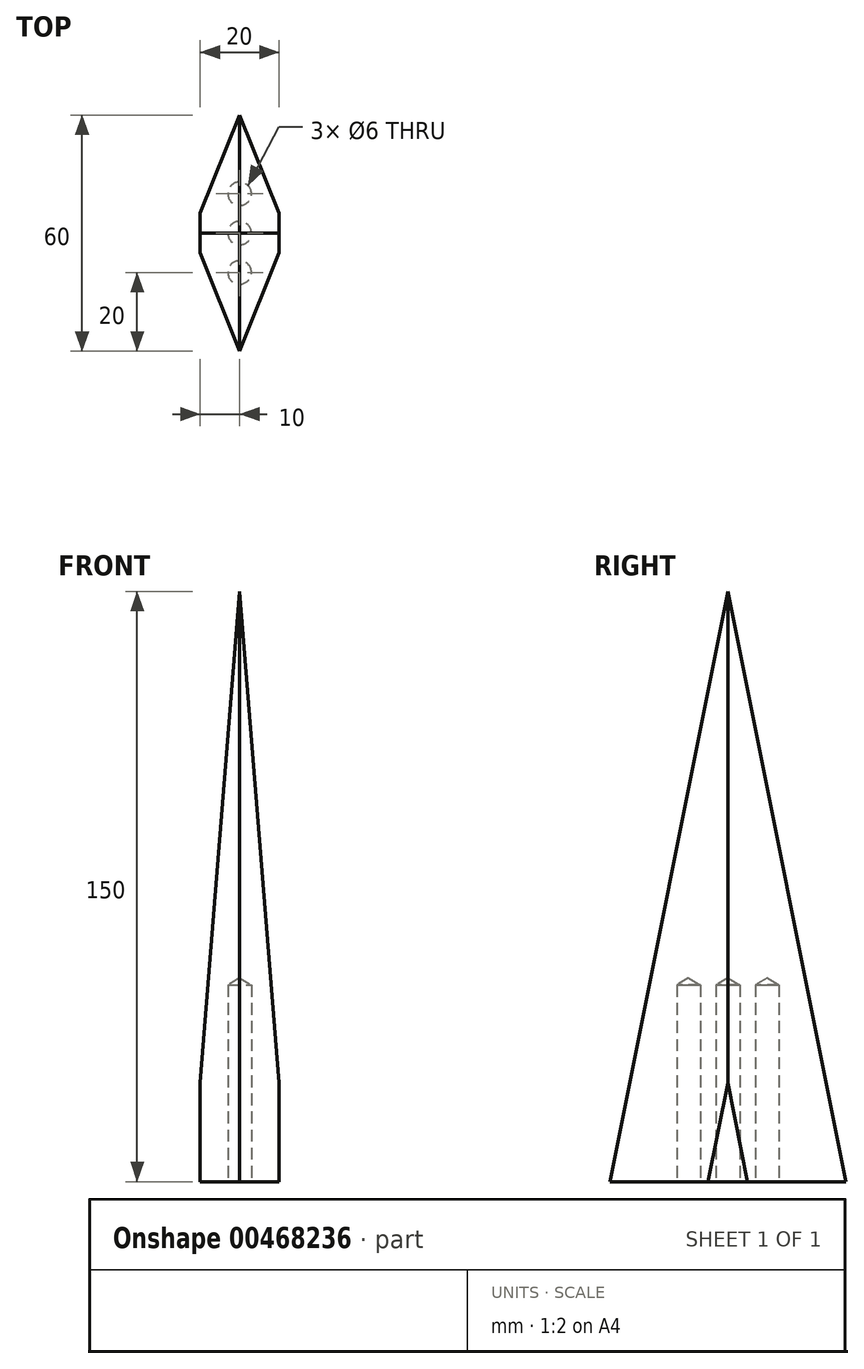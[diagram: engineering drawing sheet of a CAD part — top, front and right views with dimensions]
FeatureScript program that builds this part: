
annotation { "Feature Type Name" : "Feature", "Feature Type Description" : "" }
export const myFeature = defineFeature(function(context is Context, id is Id, definition is map)
    precondition{}
    {
        {
            var Q0;
            Q0=qCreatedBy(makeId("Top.planeOp"),FACE);
            var sketch = newSketch(context, id + "F0", { "sketchPlane" : qUnion([Q0])});
            skLineSegment(sketch, "E0.bottom", {"start": v(10, -30) * mm, "end": v(-10, -30) * mm});
            skLineSegment(sketch, "E0.top", {"start": v(10, 30) * mm, "end": v(-10, 30) * mm});
            skLineSegment(sketch, "E0.left", {"start": v(10, -30) * mm, "end": v(10, 30) * mm});
            skLineSegment(sketch, "E0.right", {"start": v(-10, -30) * mm, "end": v(-10, 30) * mm});
            skPoint(sketch, "E0.middle", {"position": v(0, 0) * mm});
            skLineSegment(sketch, "E1", {"start": v(0, 0) * mm, "end": v(0, 10) * mm});
            skLineSegment(sketch, "E2", {"start": v(0, 0) * mm, "end": v(0, -10) * mm});
            skSolve(sketch);
        }
        {
            var Q0;
            Q0=makeQuery(id+"F0.imprint","IMPRINT",FACE,{"disambiguationData":[TD([[makeQuery(id+"F0.imprint","IMPRINT",EDGE,{"derivedFrom":sQuery(id+"F0.wireOp",EDGE,"E0.bottom")}),-1.0]])]});
            extrude(context, id + "F1", {"entities" : qUnion([Q0]), "depth" : 150 * mm});
        }
        {
            var Q0;
            Q0=sQuery(id+"F0.wireOp",VERTEX,"E1.end");
            var Q1;
            Q1=sQuery(id+"F0.wireOp",VERTEX,"E0.middle");
            var Q2;
            Q2=sQuery(id+"F0.wireOp",VERTEX,"E2.end");
            var Q3;
            Q3=makeQuery(id+"F1.opExtrude","SWEPT_BODY",BODY,{"disambiguationData":[OSD([sQuery(id+"F0.wireOp",EDGE,"E0.bottom"),sQuery(id+"F0.wireOp",EDGE,"E0.top"),sQuery(id+"F0.wireOp",EDGE,"E0.left"),sQuery(id+"F0.wireOp",EDGE,"E0.right")])]});
            hole(context, id + "F2", {"style" : HoleStyle.SIMPLE, "endStyle" : HoleEndStyle.BLIND, "oppositeDirection" : true, "holeDiameter" : 6 * mm, "holeDepth" : 50 * mm, "isTappedThrough" : true, "tappedDepth" : 12 * mm, "tapClearance" : 3, "locations" : qUnion([Q0, Q1, Q2]), "scope" : qUnion([Q3])});
        }
        {
            var Q0;
            Q0=makeQuery(id+"F1.opExtrude","CAP_EDGE",EDGE,{"disambiguationData":[OSD([sQuery(id+"F0.wireOp",EDGE,"E0.bottom")])],"isStart":false});
            var Q1;
            Q1=makeQuery(id+"F1.opExtrude","CAP_EDGE",EDGE,{"disambiguationData":[OSD([sQuery(id+"F0.wireOp",EDGE,"E0.top")])],"isStart":false});
            chamfer(context, id + "F3", {"entities" : qUnion([Q0, Q1]), "chamferType" : ChamferType.TWO_OFFSETS, "width1" : 150 * mm, "oppositeDirection" : false, "width2" : 30 * mm, "tangentPropagation" : true});
        }
        {
            var Q0;
            Q0=makeQuery(id+"F3.opChamfer","BLEND_EDGE",EDGE,{"blendedFrom":[makeQuery(id+"F1.opExtrude","CAP_EDGE",EDGE,{"disambiguationData":[OSD([sQuery(id+"F0.wireOp",EDGE,"E0.bottom")])],"isStart":false}),makeQuery(id+"F1.opExtrude","SWEPT_FACE",FACE,{"disambiguationData":[OSD([sQuery(id+"F0.wireOp",EDGE,"E0.left")])]})],"blendedInto":[makeQuery(id+"F1.opExtrude","SWEPT_FACE",FACE,{"disambiguationData":[OSD([sQuery(id+"F0.wireOp",EDGE,"E0.left")])]})]});
            var Q1;
            Q1=makeQuery(id+"F3.opChamfer","BLEND_EDGE",EDGE,{"blendedFrom":[makeQuery(id+"F1.opExtrude","CAP_EDGE",EDGE,{"disambiguationData":[OSD([sQuery(id+"F0.wireOp",EDGE,"E0.top")])],"isStart":false}),makeQuery(id+"F1.opExtrude","SWEPT_FACE",FACE,{"disambiguationData":[OSD([sQuery(id+"F0.wireOp",EDGE,"E0.left")])]})],"blendedInto":[makeQuery(id+"F1.opExtrude","SWEPT_FACE",FACE,{"disambiguationData":[OSD([sQuery(id+"F0.wireOp",EDGE,"E0.left")])]})]});
            var Q2;
            Q2=makeQuery(id+"F3.opChamfer","BLEND_EDGE",EDGE,{"blendedFrom":[makeQuery(id+"F1.opExtrude","CAP_EDGE",EDGE,{"disambiguationData":[OSD([sQuery(id+"F0.wireOp",EDGE,"E0.top")])],"isStart":false}),makeQuery(id+"F1.opExtrude","SWEPT_FACE",FACE,{"disambiguationData":[OSD([sQuery(id+"F0.wireOp",EDGE,"E0.right")])]})],"blendedInto":[makeQuery(id+"F1.opExtrude","SWEPT_FACE",FACE,{"disambiguationData":[OSD([sQuery(id+"F0.wireOp",EDGE,"E0.right")])]})]});
            var Q3;
            Q3=makeQuery(id+"F3.opChamfer","BLEND_EDGE",EDGE,{"blendedFrom":[makeQuery(id+"F1.opExtrude","CAP_EDGE",EDGE,{"disambiguationData":[OSD([sQuery(id+"F0.wireOp",EDGE,"E0.bottom")])],"isStart":false}),makeQuery(id+"F1.opExtrude","SWEPT_FACE",FACE,{"disambiguationData":[OSD([sQuery(id+"F0.wireOp",EDGE,"E0.right")])]})],"blendedInto":[makeQuery(id+"F1.opExtrude","SWEPT_FACE",FACE,{"disambiguationData":[OSD([sQuery(id+"F0.wireOp",EDGE,"E0.right")])]})]});
            chamfer(context, id + "F4", {"entities" : qUnion([Q0, Q1, Q2, Q3]), "chamferType" : ChamferType.TWO_OFFSETS, "width1" : 24.5 * mm, "oppositeDirection" : false, "width2" : 10 * mm, "tangentPropagation" : true});
        }
    });
